# Revit family: Shower-Valve_Trim-KOHLER-Singulier-K-10879IN
name_source: partatom
category: Specialty Equipment
revit_build: Autodesk Revit 2017 (Build: 20160225_1515(x64)
units: mm (PartAtom-declared; Revit-internal decimal feet)

## family parameters
Cut with Voids When Loaded = No
Host = Face
OmniClass Number = 23.31.25.00
OmniClass Title = Toilet and Bath Specialties
Part Type = Normal
Room Calculation Point = No
Round Connector Dimension = Use Diameter
Shared = No

## types (4) — shared parameters
ADA Compliant = No
Assembly Code = C1030200
Date Modified = 10/05/2020
Default Elevation = 42"
Height = 6 11/16"
Length = 2 5/8"
Manufacturer = KOHLER Co.
Master Format 2014 = 10 28 00
Master Format 2014 Name = Toilet, Bath, and Laundry Accessories
Material = Metal construction
Product Documentation Link = http://resources.kohler.com
Product Name = Singulier
Product Page URL = https://www.kohler.co.in
URL = https://www.kohler.co.in
WaterSense Certified = No
Width = 4 1/2"

## per-type parameters (varying)
| type | Description | Finish | Model | Type |
| PGD- Vibrant moderne polished gold | Recessed bath and shower faucet trim with lever handle and diverter button | Kohler-Metal-PGD-Modern_Polished_Gold | K-10879IN-CP | 1 |
| 4, AF- French gold | Singulier bath and shower trim | Kohler-Metal-AF-Vibrant_French_Gold | K-10879IN-4-AF | 2 |
| 4FP, AF- French gold | Recessed bath and shower faucet trim with lever handle and diverter button | Kohler-Metal-AF-Vibrant_French_Gold | K-10879IN-4FP-AF | 3 |
| 4FP, CP- Polished chrome | Recessed bath and shower faucet trim with lever handle and diverter button | Kohler-Metal-CP-Polished_Chrome | K-10879IN-4FP-CP | 4 |

## geometry (parser evidence)
native form markers: Sweep x5
no freeform markers — native parametric forms only
